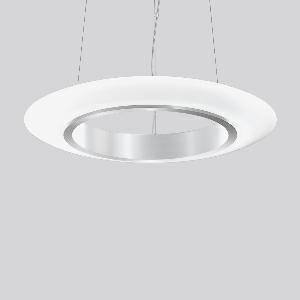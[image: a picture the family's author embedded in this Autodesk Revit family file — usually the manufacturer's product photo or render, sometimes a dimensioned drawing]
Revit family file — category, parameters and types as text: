
# Revit family: ring_of_fire_p_311570_004_1_76_1da4
name_source: partatom
category: Lighting Fixtures
units: mm (PartAtom-declared; Revit-internal decimal feet)

## family parameters
Cut with Voids When Loaded = No
Host = Face
Light Source = No
Part Type = Normal
Room Calculation Point = No
Round Connector Dimension = Use Diameter
Shared = No

## types (1)
- RING OF FIRE P (1 x LED Modul 840, 4150 lm, 4000)
    Apparent Load = 37 VA
    CIE Flux Codes = 43 73 90 55 100
    Color Rendering = 80
    Color Temperature = 4000
    Default Elevation = 1800 mm
    Description = Series: RING OF FIRE
A uniquely shaped pendant luminaire with elliptical glass. Supporting ring made of anodised aluminium. Canopy aluminium anodised. Opal glass: mouth-blown, satin finish. Suitable for pendant. 3-point steel cable suspension, steplessly adjustable. Special lengths available on request. For pendant lengths of up to 2 m, power is supplied through a suspension cable. For pendant lengths of 2 m and more, power must be supplied through a separate cable. Converter integrated in the canopy. TouchDim sensor capable. Light and/or presence sensors can be integrated. 
Colour: anodised aluminium
Diameter: 690 mm
Height: 81 mm
Suspension length: 500-1200 mm
Lamp: LED
Socket: without socket
Colour temperature: 4000K
Colour rendering index (CRI): 80
System power: 37 W
Rated luminous flux: 4150 lm
Luminous efficiency: 112 lm/W
Control gear: Converter, dimmable, DALI
Protection class: I
Type of protection: IP 20
    Height = 81 mm
    Lamp = 1 x LED Modul 840
    Lamp Light Flux = 4150 lm
    Lamp count = 1
    Length = 690 mm
    Lifetime = 50000 h
    Luminous efficacy = 112 lm/W
    Manufacturer = RZB
    ModVariant = No
    Model = 311570.004.1.76
    Mounting Place = Ceiling
    Mounting Type = Pendant
    Number of Poles = 1
    OnlyDefault = Yes
    Power Factor = 1
    Product Name = RING OF FIRE P
    Product group = Pendant luminaires
    ProductGroupID = 902
    Protection Class = Protection class I
    Protection Degree = IP 20
    RLX_Detail_Level = 1
    RLX_Emergency_Light_Flux = 0 lm
    RLX_Emergency_Type = 0
    RLX_Emergency_Type_DB = No
    RlxData = <blob elided: 30437 chars, md5=c5bfd0cd>
    Socket = socket
    Standby Power = 0 W
    System Light Flux = 4150 lm
    System Power = 37 W
    Type Comments = Product without accessories
    Type Image = 311570.004.jpg
    URL = http://relux.com
    VarID = ---
    Voltage = 230 V
    Voltage Range = 220-240 V
    Weight = 0.00 kg
    Width = 0 mm  [stored 0 ft]

note: [stored X ft] marks values corroborated as IEEE doubles in the binary element streams (Revit-internal decimal feet)

## geometry (parser evidence)
native form markers: Blend x4, Sweep x13
no freeform markers — native parametric forms only
